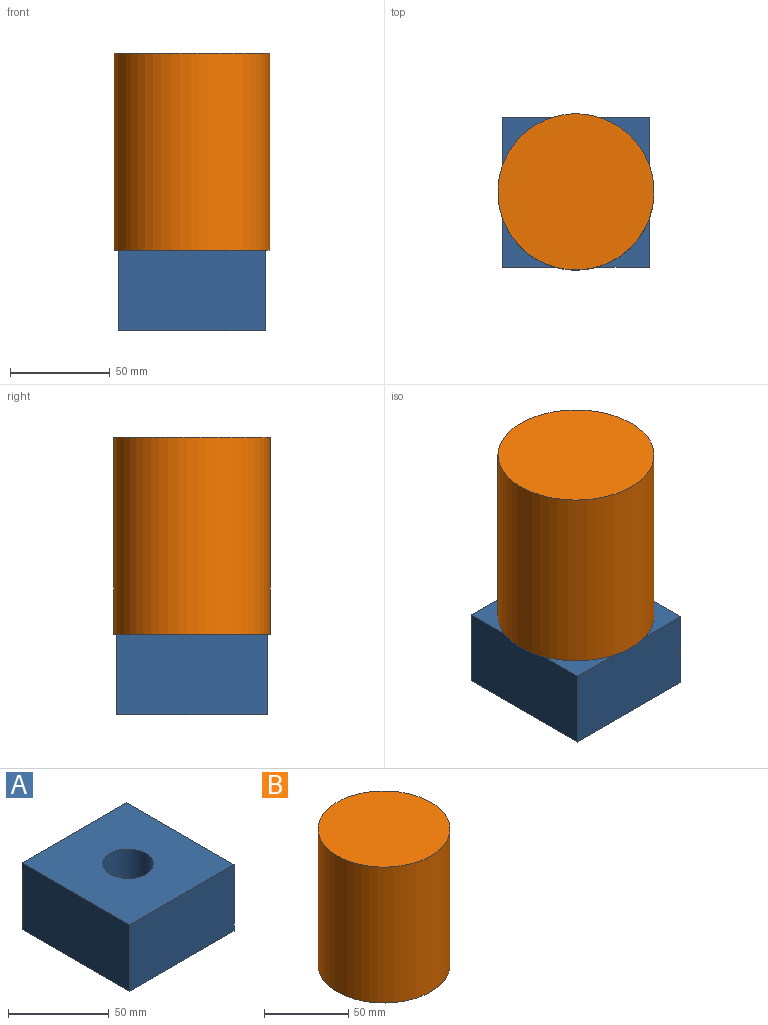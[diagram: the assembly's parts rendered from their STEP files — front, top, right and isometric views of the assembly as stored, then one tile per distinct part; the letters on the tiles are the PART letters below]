
ASSEMBLY  parts=2 mates=1
PART A: 7 faces, bbox 73.3x75.3x40.3 mm
  f0: plane 73.26x40.3mm, normal (0,1,0), area 2952.4mm2, adj f1,f4,f5,f6
  f1: plane 75.28x40.3mm, normal (-1,0,0), area 3033.7mm2, adj f0,f2,f5,f6
  f2: plane 73.26x40.3mm, normal (0,-1,0), area 2952.4mm2, adj f1,f4,f5,f6
  f3: cylinder r=12.63mm len=40.3mm, axis (0,0,-1), area 3196.9mm2, adj f5,f6
  f4: plane 75.28x40.3mm, normal (1,0,0), area 3033.7mm2, adj f0,f2,f5,f6
  f5: plane 75.28x73.26mm, normal (0,0,1), area 5014.1mm2, adj f0,f1,f2,f3,f4
  f6: plane 75.28x73.26mm, normal (0,0,-1), area 5014.1mm2, adj f0,f1,f2,f3,f4
PART B: 3 faces, bbox 78.2x78.2x98.6 mm
  f0: cylinder r=39.1mm len=98.6mm, axis (0,0,-1), area 24222.1mm2, adj f1,f2
  f1: plane 78.2x78.2mm, normal (0,0,1), area 4802.4mm2, adj f0
  f2: plane 78.2x78.2mm, normal (0,0,-1), area 4802.4mm2, adj f0
PLACE A at identity
PLACE B t=(0,0,40.3)mm
MATE fastened B.f0 <-> A.f3  axis (0,0,-1) through (0,0,40.3)mm
